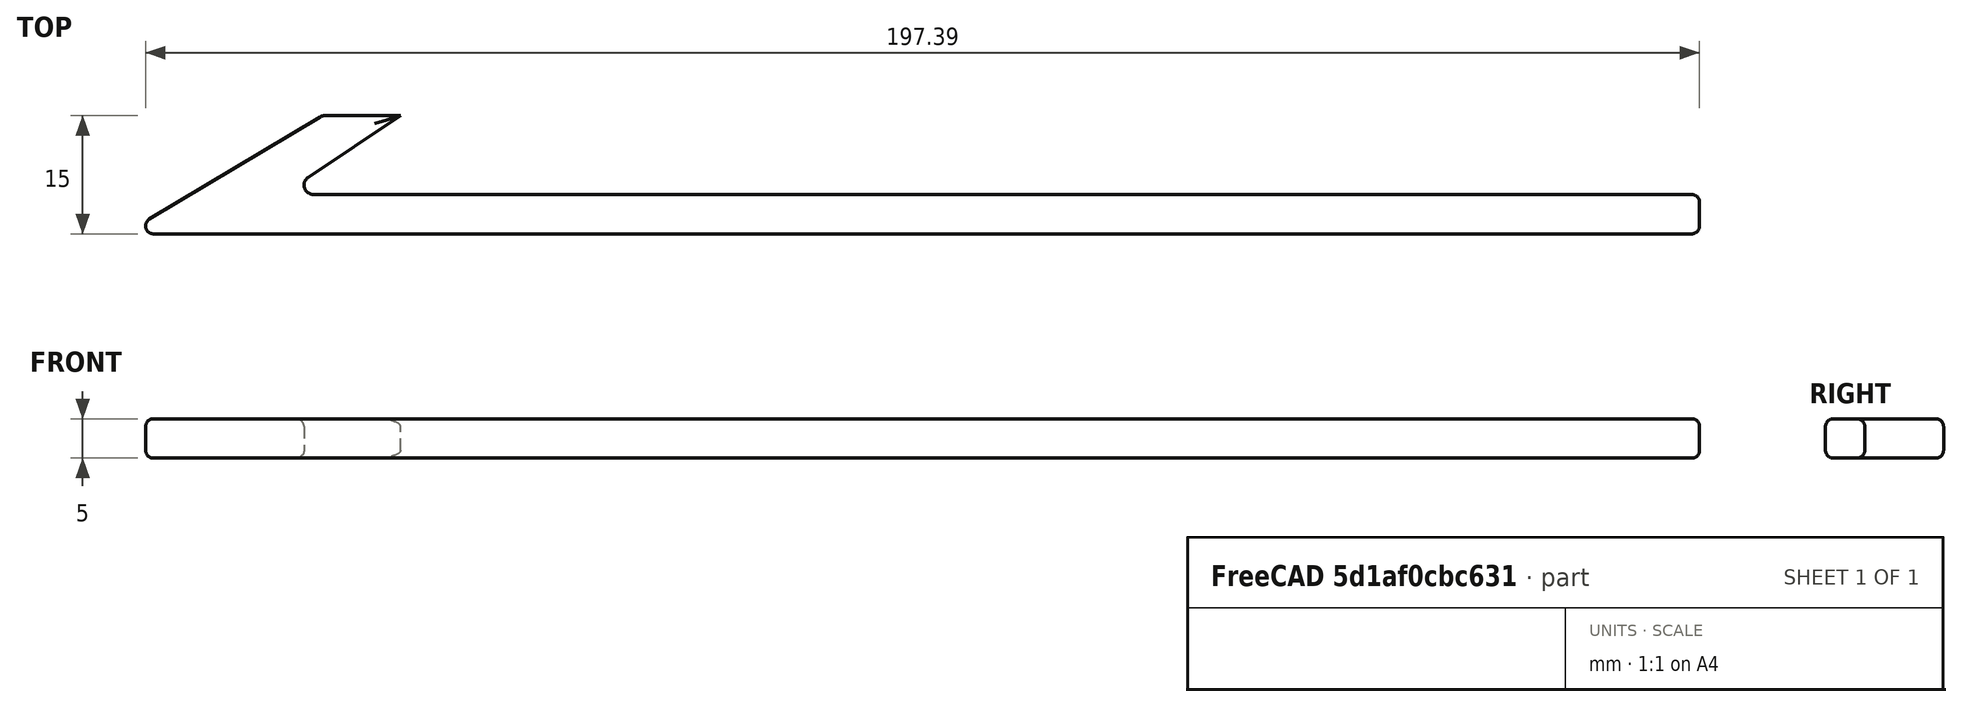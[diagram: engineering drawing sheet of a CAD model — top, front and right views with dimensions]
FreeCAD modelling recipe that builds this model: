
FCSTD DOCUMENT  (FreeCAD 0.14R3702 (Git))
Label: grab-hook
License: CC-BY 3.0
LicenseURL: http://creativecommons.org/licenses/by/3.0/
objects: Sketcher::SketchObject×1, Part::Extrusion×1, Part::Fillet×1
note: 3 computed .brp shape members not serialized (recipe doc carries the construction recipe); baked Part::Feature solids carry a one-line shape summary decoded from their .brp

FEATURE [Sketcher::SketchObject] Sketch
  sketch-geometry (7):
    g0: LineSegment StartX=0 StartY=0 StartZ=0 EndX=200 EndY=0 EndZ=0
    g1: LineSegment StartX=200 StartY=5 StartZ=0 EndX=200 EndY=0 EndZ=0
    g2: LineSegment StartX=0 StartY=0 StartZ=0 EndX=25 EndY=15 EndZ=0
    g3: LineSegment StartX=25 StartY=15 StartZ=0 EndX=35 EndY=15 EndZ=0
    g4: LineSegment StartX=35 StartY=15 StartZ=0 EndX=23.2648 EndY=7.17656 EndZ=0
    g5: LineSegment StartX=23.9238 StartY=5 StartZ=0 EndX=200 EndY=5 EndZ=0
    g6: ArcOfCircle CenterX=23.9238 CenterY=6.18804 CenterZ=0 NormalX=0 NormalY=0 NormalZ=1 Radius=1.18805 StartAngle=2.1588 EndAngle=4.71239
  constraints (11):
    c: Coincident(g0,g-1)
    c: Horizontal(g0)
    c: Coincident(g1,g0)
    c: Vertical(g1)
    c: Coincident(g2,g-1)
    c: Coincident(g3,g2)
    c: Horizontal(g3)
    c: Coincident(g4,g3)
    c: Tangent(g4,g6)
    c: Tangent(g5,g6)
    c: Horizontal(g5)
FEATURE [Part::Extrusion] Extrude
  Base = -> Sketch
  Dir = (0,0,5)
  Solid = true
FEATURE [Part::Fillet] Fillet
  Base = -> Extrude
  Edges = 18 edges r=1: [Edge1,Edge2,Edge3,Edge4,Edge5,Edge6,Edge7,Edge9,Edge10,Edge12,Edge13,Edge15,Edge16,Edge17,Edge18,Edge19,Edge20,Edge21]
